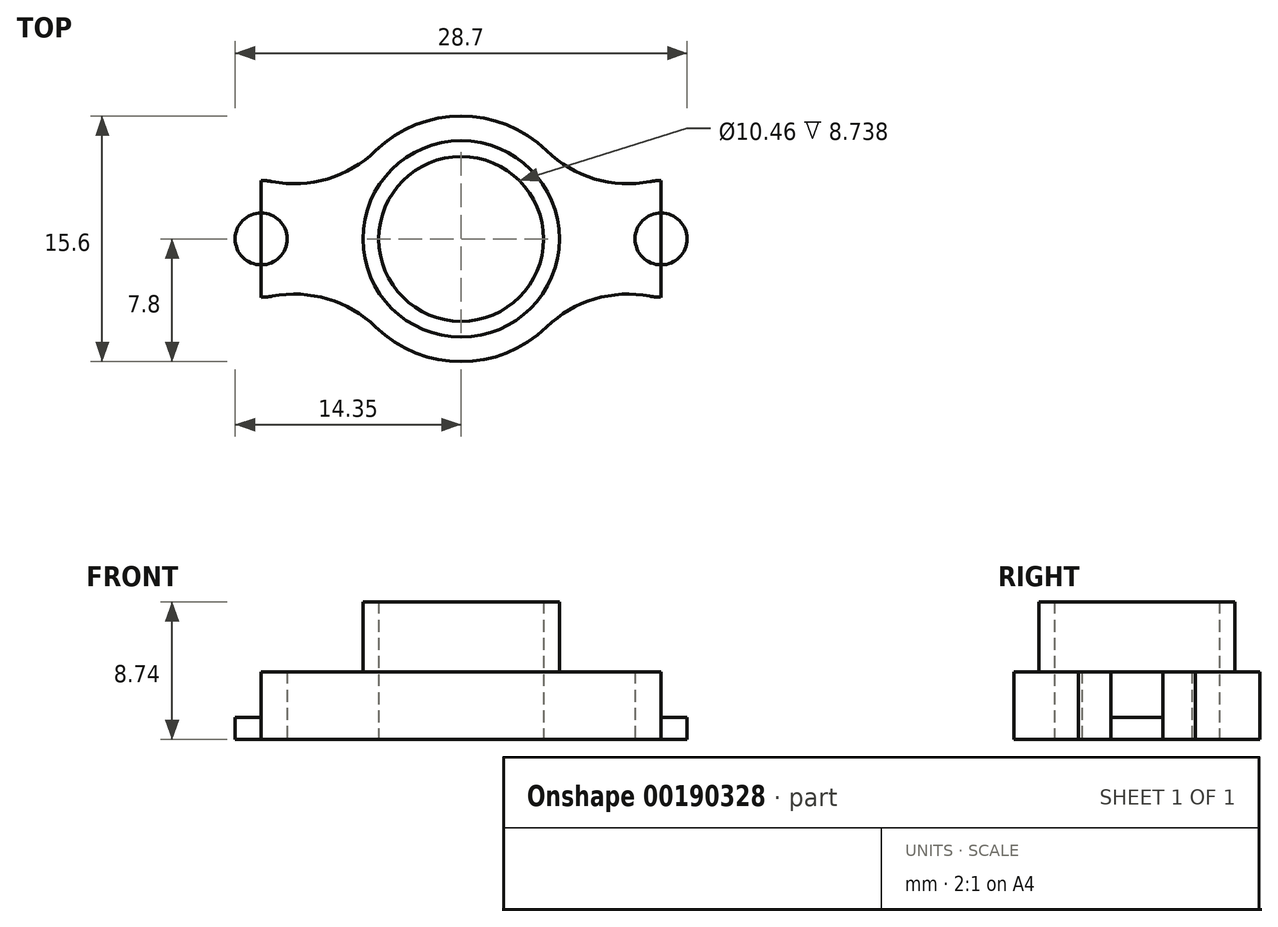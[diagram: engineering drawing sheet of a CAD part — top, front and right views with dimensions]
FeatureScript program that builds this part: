
annotation { "Feature Type Name" : "Feature", "Feature Type Description" : "" }
export const myFeature = defineFeature(function(context is Context, id is Id, definition is map)
    precondition{}
    {
        {
            var Q0;
            Q0=qCreatedBy(makeId("Top.planeOp"),FACE);
            var sketch = newSketch(context, id + "F0", { "sketchPlane" : qUnion([Q0])});
            skCircle(sketch, "E0", {"center": v(0, 0) * mm, "radius": 6.24 * mm});
            skCircle(sketch, "E1", {"center": v(0, 0) * mm, "radius": 5.23 * mm});
            skCircle(sketch, "E2", {"center": v(-12.7, 0) * mm, "radius": 1.65 * mm});
            skCircle(sketch, "E3", {"center": v(12.7, 0) * mm, "radius": 1.65 * mm});
            skArc(sketch, "E4", {"start": v(-12, 3.64) * mm, "mid": v(-8.47, 3.82) * mm, "end": v(-5.43, 5.6) * mm});
            skArc(sketch, "E5", {"start": v(5.43, 5.6) * mm, "mid": v(0, 7.8) * mm, "end": v(-5.43, 5.6) * mm});
            skArc(sketch, "E6", {"start": v(5.43, 5.6) * mm, "mid": v(8.47, 3.82) * mm, "end": v(12, 3.64) * mm});
            skArc(sketch, "E7", {"start": v(12, -3.64) * mm, "mid": v(16.4, 0) * mm, "end": v(12, 3.64) * mm});
            skArc(sketch, "E8", {"start": v(12, -3.64) * mm, "mid": v(8.47, -3.82) * mm, "end": v(5.43, -5.6) * mm});
            skArc(sketch, "E9", {"start": v(-5.43, -5.6) * mm, "mid": v(0, -7.8) * mm, "end": v(5.43, -5.6) * mm});
            skArc(sketch, "E10", {"start": v(-5.43, -5.6) * mm, "mid": v(-8.47, -3.82) * mm, "end": v(-12, -3.64) * mm});
            skArc(sketch, "E11", {"start": v(-12, 3.64) * mm, "mid": v(-16.4, 0) * mm, "end": v(-12, -3.64) * mm});
            skCircle(sketch, "E12", {"center": v(0, 0) * mm, "radius": 4.19 * mm});
            skLineSegment(sketch, "E13", {"start": v(-20.02, 0) * mm, "end": v(20.02, 0) * mm});
            skLineSegment(sketch, "E14", {"start": v(12.7, -5.34) * mm, "end": v(12.7, 5.34) * mm});
            skLineSegment(sketch, "E15", {"start": v(-12.7, -5.34) * mm, "end": v(-12.7, 5.34) * mm});
            skLineSegment(sketch, "E16", {"start": v(0, -11.23) * mm, "end": v(0, 11.23) * mm});
            skSolve(sketch);
        }
        {
            var Q0;
            {var subQ10=sQuery(id+"F0.wireOp",EDGE,"E4");Q0=makeQuery(id+"F0.imprint","IMPRINT",FACE,{"disambiguationData":[TD([[makeQuery(id+"F0.imprint","IMPRINT",EDGE,{"derivedFrom":subQ10}),-1.0]])]});}
            var Q1;
            {var subQ0=sQuery(id+"F0.wireOp",EDGE,"E13");var subQ1=sQuery(id+"F0.wireOp",EDGE,"E2");var subQ2=makeQuery(id+"F0.imprint","INTERSECT",VERTEX,{"disambiguationData":[OD(1.0)],"derivedFrom":[subQ1,subQ0]});Q1=makeQuery(id+"F0.imprint","IMPRINT",FACE,{"disambiguationData":[TD([[makeQuery(id+"F0.imprint","IMPRINT",EDGE,{"disambiguationData":[TD([[subQ2,-1.0]])],"derivedFrom":subQ1}),1.0]])]});}
            var Q2;
            {var subQ0=sQuery(id+"F0.wireOp",EDGE,"E15");var subQ1=sQuery(id+"F0.wireOp",EDGE,"E2");var subQ2=makeQuery(id+"F0.imprint","INTERSECT",VERTEX,{"disambiguationData":[OD(0.0)],"derivedFrom":[subQ1,subQ0]});Q2=makeQuery(id+"F0.imprint","IMPRINT",FACE,{"disambiguationData":[TD([[makeQuery(id+"F0.imprint","IMPRINT",EDGE,{"disambiguationData":[TD([[subQ2,-1.0]])],"derivedFrom":subQ1}),1.0]])]});}
            var Q3;
            {var subQ0=sQuery(id+"F0.wireOp",EDGE,"E10");Q3=makeQuery(id+"F0.imprint","IMPRINT",FACE,{"disambiguationData":[TD([[makeQuery(id+"F0.imprint","IMPRINT",EDGE,{"derivedFrom":subQ0}),-1.0]])]});}
            var Q4;
            {var subQ0=sQuery(id+"F0.wireOp",EDGE,"E16");var subQ1=sQuery(id+"F0.wireOp",EDGE,"E0");var subQ2=makeQuery(id+"F0.imprint","INTERSECT",VERTEX,{"disambiguationData":[OD(0.0)],"derivedFrom":[subQ1,subQ0]});Q4=makeQuery(id+"F0.imprint","IMPRINT",FACE,{"disambiguationData":[TD([[makeQuery(id+"F0.imprint","IMPRINT",EDGE,{"disambiguationData":[TD([[subQ2,1.0]])],"derivedFrom":subQ1}),-1.0]])]});}
            var Q5;
            {var subQ0=sQuery(id+"F0.wireOp",EDGE,"E16");var subQ1=sQuery(id+"F0.wireOp",EDGE,"E0");var subQ2=makeQuery(id+"F0.imprint","INTERSECT",VERTEX,{"disambiguationData":[OD(0.0)],"derivedFrom":[subQ1,subQ0]});Q5=makeQuery(id+"F0.imprint","IMPRINT",FACE,{"disambiguationData":[TD([[makeQuery(id+"F0.imprint","IMPRINT",EDGE,{"disambiguationData":[TD([[subQ2,-1.0]])],"derivedFrom":subQ1}),-1.0]])]});}
            var Q6;
            {var subQ0=sQuery(id+"F0.wireOp",EDGE,"E13");var subQ1=sQuery(id+"F0.wireOp",EDGE,"E0");var subQ2=makeQuery(id+"F0.imprint","INTERSECT",VERTEX,{"disambiguationData":[OD(1.0)],"derivedFrom":[subQ1,subQ0]});Q6=makeQuery(id+"F0.imprint","IMPRINT",FACE,{"disambiguationData":[TD([[makeQuery(id+"F0.imprint","IMPRINT",EDGE,{"disambiguationData":[TD([[subQ2,-1.0]])],"derivedFrom":subQ1}),-1.0]])]});}
            var Q7;
            {var subQ0=sQuery(id+"F0.wireOp",EDGE,"E13");var subQ1=sQuery(id+"F0.wireOp",EDGE,"E0");var subQ2=makeQuery(id+"F0.imprint","INTERSECT",VERTEX,{"disambiguationData":[OD(0.0)],"derivedFrom":[subQ1,subQ0]});Q7=makeQuery(id+"F0.imprint","IMPRINT",FACE,{"disambiguationData":[TD([[makeQuery(id+"F0.imprint","IMPRINT",EDGE,{"disambiguationData":[TD([[subQ2,1.0]])],"derivedFrom":subQ1}),-1.0]])]});}
            var Q8;
            {var subQ0=sQuery(id+"F0.wireOp",EDGE,"E6");Q8=makeQuery(id+"F0.imprint","IMPRINT",FACE,{"disambiguationData":[TD([[makeQuery(id+"F0.imprint","IMPRINT",EDGE,{"derivedFrom":subQ0}),-1.0]])]});}
            var Q9;
            {var subQ0=sQuery(id+"F0.wireOp",EDGE,"E8");Q9=makeQuery(id+"F0.imprint","IMPRINT",FACE,{"disambiguationData":[TD([[makeQuery(id+"F0.imprint","IMPRINT",EDGE,{"derivedFrom":subQ0}),-1.0]])]});}
            var Q10;
            {var subQ0=sQuery(id+"F0.wireOp",EDGE,"E14");var subQ1=sQuery(id+"F0.wireOp",EDGE,"E3");var subQ2=makeQuery(id+"F0.imprint","INTERSECT",VERTEX,{"disambiguationData":[OD(0.0)],"derivedFrom":[subQ1,subQ0]});Q10=makeQuery(id+"F0.imprint","IMPRINT",FACE,{"disambiguationData":[TD([[makeQuery(id+"F0.imprint","IMPRINT",EDGE,{"disambiguationData":[TD([[subQ2,1.0]])],"derivedFrom":subQ1}),1.0]])]});}
            var Q11;
            {var subQ0=sQuery(id+"F0.wireOp",EDGE,"E13");var subQ1=sQuery(id+"F0.wireOp",EDGE,"E3");var subQ2=makeQuery(id+"F0.imprint","INTERSECT",VERTEX,{"disambiguationData":[OD(0.0)],"derivedFrom":[subQ1,subQ0]});Q11=makeQuery(id+"F0.imprint","IMPRINT",FACE,{"disambiguationData":[TD([[makeQuery(id+"F0.imprint","IMPRINT",EDGE,{"disambiguationData":[TD([[subQ2,1.0]])],"derivedFrom":subQ1}),1.0]])]});}
            extrude(context, id + "F1", {"entities" : qUnion([Q0, Q1, Q2, Q3, Q4, Q5, Q6, Q7, Q8, Q9, Q10, Q11]), "depth" : 1.4 * mm});
        }
        {
            var Q0;
            {var subQ0=sQuery(id+"F0.wireOp",EDGE,"E13");var subQ1=sQuery(id+"F0.wireOp",EDGE,"E1");var subQ2=makeQuery(id+"F0.imprint","INTERSECT",VERTEX,{"disambiguationData":[OD(1.0)],"derivedFrom":[subQ1,subQ0]});Q0=makeQuery(id+"F0.imprint","IMPRINT",FACE,{"disambiguationData":[TD([[makeQuery(id+"F0.imprint","IMPRINT",EDGE,{"disambiguationData":[TD([[subQ2,-1.0]])],"derivedFrom":subQ1}),-1.0]])]});}
            var Q1;
            {var subQ0=sQuery(id+"F0.wireOp",EDGE,"E13");var subQ1=sQuery(id+"F0.wireOp",EDGE,"E1");var subQ2=makeQuery(id+"F0.imprint","INTERSECT",VERTEX,{"disambiguationData":[OD(0.0)],"derivedFrom":[subQ1,subQ0]});Q1=makeQuery(id+"F0.imprint","IMPRINT",FACE,{"disambiguationData":[TD([[makeQuery(id+"F0.imprint","IMPRINT",EDGE,{"disambiguationData":[TD([[subQ2,1.0]])],"derivedFrom":subQ1}),-1.0]])]});}
            var Q2;
            {var subQ0=sQuery(id+"F0.wireOp",EDGE,"E16");var subQ1=sQuery(id+"F0.wireOp",EDGE,"E1");var subQ2=makeQuery(id+"F0.imprint","INTERSECT",VERTEX,{"disambiguationData":[OD(0.0)],"derivedFrom":[subQ1,subQ0]});Q2=makeQuery(id+"F0.imprint","IMPRINT",FACE,{"disambiguationData":[TD([[makeQuery(id+"F0.imprint","IMPRINT",EDGE,{"disambiguationData":[TD([[subQ2,1.0]])],"derivedFrom":subQ1}),-1.0]])]});}
            var Q3;
            {var subQ0=sQuery(id+"F0.wireOp",EDGE,"E16");var subQ1=sQuery(id+"F0.wireOp",EDGE,"E1");var subQ2=makeQuery(id+"F0.imprint","INTERSECT",VERTEX,{"disambiguationData":[OD(0.0)],"derivedFrom":[subQ1,subQ0]});Q3=makeQuery(id+"F0.imprint","IMPRINT",FACE,{"disambiguationData":[TD([[makeQuery(id+"F0.imprint","IMPRINT",EDGE,{"disambiguationData":[TD([[subQ2,-1.0]])],"derivedFrom":subQ1}),-1.0]])]});}
            extrude(context, id + "F2", {"entities" : qUnion([Q0, Q1, Q2, Q3]), "operationType" : NewBodyOperationType.ADD, "depth" : 8.74 * mm});
        }
        {
            var Q0;
            {var subQ0=sQuery(id+"F0.wireOp",EDGE,"E16");var subQ1=sQuery(id+"F0.wireOp",EDGE,"E0");var subQ2=makeQuery(id+"F0.imprint","INTERSECT",VERTEX,{"disambiguationData":[OD(0.0)],"derivedFrom":[subQ1,subQ0]});Q0=makeQuery(id+"F0.imprint","IMPRINT",FACE,{"disambiguationData":[TD([[makeQuery(id+"F0.imprint","IMPRINT",EDGE,{"disambiguationData":[TD([[subQ2,-1.0]])],"derivedFrom":subQ1}),-1.0]])]});}
            var Q1;
            {var subQ0=sQuery(id+"F0.wireOp",EDGE,"E16");var subQ1=sQuery(id+"F0.wireOp",EDGE,"E0");var subQ2=makeQuery(id+"F0.imprint","INTERSECT",VERTEX,{"disambiguationData":[OD(0.0)],"derivedFrom":[subQ1,subQ0]});Q1=makeQuery(id+"F0.imprint","IMPRINT",FACE,{"disambiguationData":[TD([[makeQuery(id+"F0.imprint","IMPRINT",EDGE,{"disambiguationData":[TD([[subQ2,1.0]])],"derivedFrom":subQ1}),-1.0]])]});}
            var Q2;
            {var subQ0=sQuery(id+"F0.wireOp",EDGE,"E13");var subQ1=sQuery(id+"F0.wireOp",EDGE,"E0");var subQ2=makeQuery(id+"F0.imprint","INTERSECT",VERTEX,{"disambiguationData":[OD(0.0)],"derivedFrom":[subQ1,subQ0]});Q2=makeQuery(id+"F0.imprint","IMPRINT",FACE,{"disambiguationData":[TD([[makeQuery(id+"F0.imprint","IMPRINT",EDGE,{"disambiguationData":[TD([[subQ2,1.0]])],"derivedFrom":subQ1}),-1.0]])]});}
            var Q3;
            {var subQ0=sQuery(id+"F0.wireOp",EDGE,"E13");var subQ1=sQuery(id+"F0.wireOp",EDGE,"E0");var subQ2=makeQuery(id+"F0.imprint","INTERSECT",VERTEX,{"disambiguationData":[OD(1.0)],"derivedFrom":[subQ1,subQ0]});Q3=makeQuery(id+"F0.imprint","IMPRINT",FACE,{"disambiguationData":[TD([[makeQuery(id+"F0.imprint","IMPRINT",EDGE,{"disambiguationData":[TD([[subQ2,-1.0]])],"derivedFrom":subQ1}),-1.0]])]});}
            extrude(context, id + "F3", {"entities" : qUnion([Q0, Q1, Q2, Q3]), "operationType" : NewBodyOperationType.ADD, "depth" : 4.3 * mm});
        }
    });
